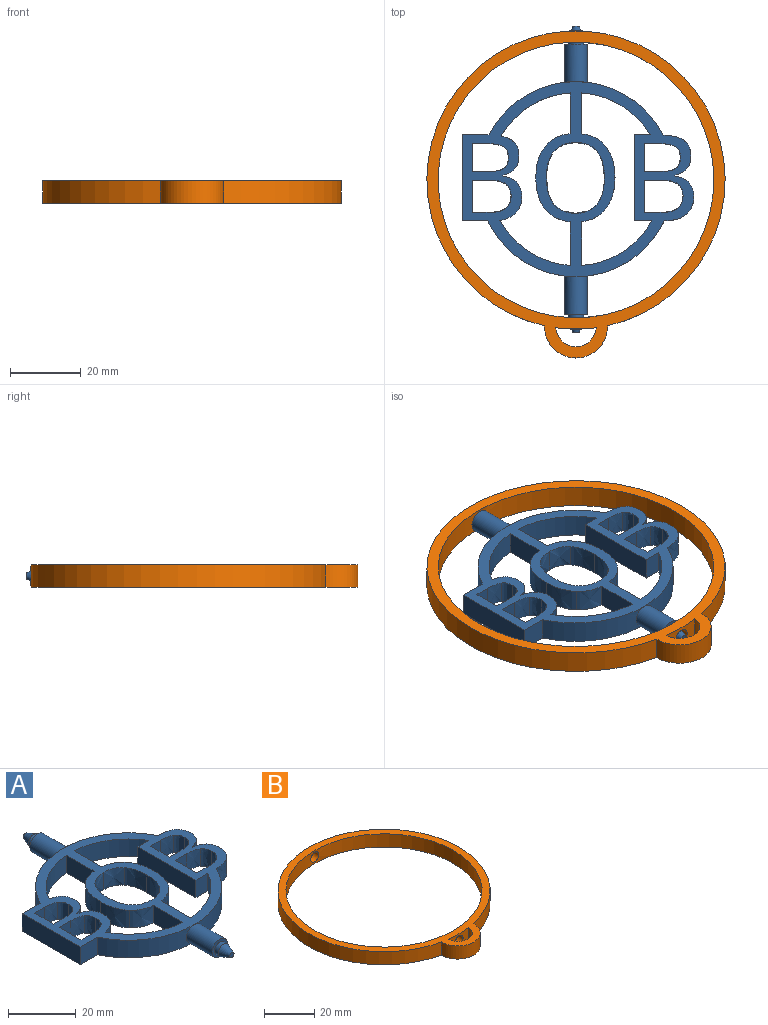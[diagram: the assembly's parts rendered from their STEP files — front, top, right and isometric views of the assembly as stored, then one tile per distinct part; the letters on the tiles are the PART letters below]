
ASSEMBLY  parts=2 mates=1
PART A: 91 faces, bbox 65.3x86.4x6.4 mm
  f0: cylinder r=27.5mm len=24.86mm, axis (0,0,1), area 181.3mm2, adj f34,f44,f45,f83
  f1: cylinder r=27.5mm len=24.5mm, axis (0,0,1), area 176.1mm2, adj f42,f44,f45,f82
  f2: extruded ~6.35x6.06mm, area 43.2mm2, adj f8,f44,f45,f75
  f3: extruded ~6.35x6.09mm, area 43.4mm2, adj f10,f44,f45,f76
  f4: cylinder r=24.36mm len=19.45mm, axis (0,0,1), area 151.6mm2, adj f19,f44,f45,f72
  f5: cylinder r=24.36mm len=19.84mm, axis (0,0,1), area 156.2mm2, adj f6,f18,f44,f45
  f6: plane 12.28x6.35mm, normal (-1,0,0), area 78mm2, adj f5,f9,f44,f45
  f7: extruded ~6.76x6.35mm, area 48.6mm2, adj f44,f45,f72,f79
  f8: extruded ~6.35x6.13mm, area 43.6mm2, adj f2,f44,f45,f74
  f9: extruded ~6.82x6.35mm, area 49.1mm2, adj f6,f44,f45,f80
  f10: extruded ~6.35x6.1mm, area 43.4mm2, adj f3,f44,f45,f73
  f11: cylinder r=24.36mm len=19.75mm, axis (0,0,1), area 155mm2, adj f15,f44,f45,f47
  f12: cylinder r=27.5mm len=24.86mm, axis (0,0,1), area 181.3mm2, adj f44,f45,f62,f83
  f13: cylinder r=24.36mm len=19.42mm, axis (0,0,1), area 150.2mm2, adj f44,f45,f60,f71
  f14: cylinder r=27.5mm len=24.51mm, axis (0,0,1), area 176.2mm2, adj f44,f45,f46,f82
  f15: plane 12.32x6.35mm, normal (1,0,0), area 78.2mm2, adj f11,f16,f44,f45
  f16: extruded ~6.46x6.35mm, area 47mm2, adj f15,f44,f45,f77
  f17: extruded ~6.52x6.35mm, area 47.3mm2, adj f44,f45,f71,f78
  f18: extruded ~6.35x3.96mm, area 27.6mm2, adj f5,f35,f44,f45
  f19: extruded ~6.35x2.89mm, area 19.7mm2, adj f4,f40,f44,f45
  f20: plane 9.08x6.35mm, normal (1,0,0), area 57.6mm2, adj f21,f43,f44,f45
  f21: plane 6.35x4.83mm, normal (0,-1,0), area 30.7mm2, adj f20,f22,f44,f45
  f22: extruded ~6.35x4.62mm, area 30.5mm2, adj f21,f23,f44,f45
  f23: extruded ~6.35x3.32mm, area 24.2mm2, adj f22,f24,f44,f45
  f24: extruded ~6.35x3.56mm, area 25.4mm2, adj f23,f25,f44,f45
  f25: extruded ~6.35x4.42mm, area 29.5mm2, adj f24,f43,f44,f45
  f26: plane 6.35x4.64mm, normal (0,1,0), area 29.5mm2, adj f27,f41,f44,f45
  f27: plane 7.94x6.35mm, normal (1,0,0), area 50.4mm2, adj f26,f28,f44,f45
  f28: plane 6.35x4.15mm, normal (0,-1,0), area 26.4mm2, adj f27,f29,f44,f45
  f29: extruded ~6.35x4.64mm, area 30.4mm2, adj f28,f30,f44,f45
  f30: extruded ~6.35x2.95mm, area 21.9mm2, adj f29,f31,f44,f45
  f31: extruded ~6.35x3.16mm, area 22.6mm2, adj f30,f41,f44,f45
  f32: plane 6.85x6.35mm, normal (0,1,0), area 43.5mm2, adj f33,f42,f44,f45
  f33: plane 24.25x6.35mm, normal (-1,0,0), area 154mm2, adj f32,f34,f44,f45
  f34: plane 7.21x6.35mm, normal (0,-1,0), area 45.8mm2, adj f0,f33,f44,f45
  f35: extruded ~6.35x5.07mm, area 36.4mm2, adj f18,f36,f44,f45
  f36: extruded ~6.35x5.81mm, area 56.4mm2, adj f35,f37,f44,f45
  f37: plane 6.35x0.16mm, normal (1,0,0), area 1mm2, adj f36,f38,f44,f45
  f38: extruded ~6.35x3.51mm, area 25.6mm2, adj f37,f39,f44,f45
  f39: extruded ~6.35x3.56mm, area 24.4mm2, adj f38,f40,f44,f45
  f40: extruded ~6.35x4.56mm, area 33.5mm2, adj f19,f39,f44,f45
  f41: extruded ~6.35x4.3mm, area 28.4mm2, adj f26,f31,f44,f45
  f42: extruded ~6.35x0.72mm, area 4.6mm2, adj f1,f32,f44,f45
  f43: plane 6.35x5.06mm, normal (0,1,0), area 32.2mm2, adj f20,f25,f44,f45
  f44: plane 65.27x54.99mm, normal (0,0,1), area 1015.6mm2, adj f0,f1,f2,f3,f4,f5,f6,f7
  f45: plane 65.27x54.99mm, normal (0,0,-1), area 1015.6mm2, adj f0,f1,f2,f3,f4,f5,f6,f7
  f46: extruded ~6.35x5.72mm, area 37.9mm2, adj f14,f44,f45,f68
  f47: plane 6.35x4.94mm, normal (0,-1,0), area 31.4mm2, adj f11,f44,f45,f61
  f48: plane 9.08x6.35mm, normal (1,0,0), area 57.6mm2, adj f44,f45,f49,f70
  f49: plane 6.35x4.83mm, normal (0,-1,0), area 30.7mm2, adj f44,f45,f48,f50
  f50: extruded ~6.35x4.62mm, area 30.5mm2, adj f44,f45,f49,f51
  f51: extruded ~6.35x3.32mm, area 24.2mm2, adj f44,f45,f50,f52
  f52: extruded ~6.35x3.56mm, area 25.4mm2, adj f44,f45,f51,f53
  f53: extruded ~6.35x4.42mm, area 29.5mm2, adj f44,f45,f52,f70
  f54: plane 6.35x4.64mm, normal (0,1,0), area 29.5mm2, adj f44,f45,f55,f69
  f55: plane 7.94x6.35mm, normal (1,0,0), area 50.4mm2, adj f44,f45,f54,f56
  f56: plane 6.35x4.15mm, normal (0,-1,0), area 26.4mm2, adj f44,f45,f55,f57
  f57: extruded ~6.35x4.64mm, area 30.4mm2, adj f44,f45,f56,f58
  f58: extruded ~6.35x2.95mm, area 21.9mm2, adj f44,f45,f57,f59
  f59: extruded ~6.35x3.16mm, area 22.6mm2, adj f44,f45,f58,f69
  f60: plane 6.35x4.52mm, normal (0,1,0), area 28.7mm2, adj f13,f44,f45,f61
  f61: plane 24.25x6.35mm, normal (-1,0,0), area 154mm2, adj f44,f45,f47,f60
  f62: extruded ~6.35x6.15mm, area 41.5mm2, adj f12,f44,f45,f63
  f63: extruded ~6.35x5.07mm, area 36.4mm2, adj f44,f45,f62,f64
  f64: extruded ~6.35x5.81mm, area 56.4mm2, adj f44,f45,f63,f65
  f65: plane 6.35x0.16mm, normal (1,0,0), area 1mm2, adj f44,f45,f64,f66
  f66: extruded ~6.35x3.51mm, area 25.6mm2, adj f44,f45,f65,f67
  f67: extruded ~6.35x3.56mm, area 24.4mm2, adj f44,f45,f66,f68
  f68: extruded ~6.35x4.56mm, area 33.5mm2, adj f44,f45,f46,f67
  f69: extruded ~6.35x4.3mm, area 28.4mm2, adj f44,f45,f54,f59
  f70: plane 6.35x5.06mm, normal (0,1,0), area 32.2mm2, adj f44,f45,f48,f53
  f71: plane 11.53x6.35mm, normal (1,0,0), area 73.2mm2, adj f13,f17,f44,f45
  f72: plane 11.5x6.35mm, normal (-1,0,0), area 73mm2, adj f4,f7,f44,f45
  f73: extruded ~7.47x6.35mm, area 50.3mm2, adj f10,f44,f45,f74
  f74: extruded ~7.4x6.35mm, area 49.8mm2, adj f8,f44,f45,f73
  f75: extruded ~7.42x6.35mm, area 49.8mm2, adj f2,f44,f45,f76
  f76: extruded ~7.48x6.35mm, area 50.2mm2, adj f3,f44,f45,f75
  f77: extruded ~9.16x6.35mm, area 62.5mm2, adj f16,f44,f45,f78
  f78: extruded ~9.16x6.35mm, area 62.4mm2, adj f17,f44,f45,f77
  f79: extruded ~9.18x6.35mm, area 62.6mm2, adj f7,f44,f45,f80
  f80: extruded ~9.25x6.35mm, area 63mm2, adj f9,f44,f45,f79
  f81: plane 6.35x6.35mm, normal (0,1,0), area 17mm2, adj f82,f88
  f82: cylinder r=3.17mm len=10.79mm, axis (0,1,0), area 213.4mm2, adj f1,f14,f81
  f83: cylinder r=3.17mm len=10.79mm, axis (0,1,0), area 213.4mm2, adj f0,f12,f84
  f84: plane 6.35x6.35mm, normal (0,-1,0), area 17mm2, adj f83,f85
  f85: cylinder r=2.16mm len=4.32mm, axis (0,1,0), area 21.6mm2, adj f84,f87
  f86: plane 1.78x1.78mm, normal (0,-1,0), area 2.5mm2, adj f87
  f87: cone r=0.89mm half-angle=20deg, axis (0,1,0), area 35.6mm2, adj f85,f86
  f88: cylinder r=2.16mm len=4.32mm, axis (0,-1,0), area 21.6mm2, adj f81,f90
  f89: plane 1.78x1.78mm, normal (0,1,0), area 2.5mm2, adj f90
  f90: cone r=2.16mm half-angle=20deg, axis (0,-1,0), area 35.6mm2, adj f88,f89
PART B: 9 faces, bbox 84.1x92.2x6.4 mm
  f0: cylinder r=42.04mm len=11.42mm, axis (0,0,-1), area 56.3mm2, adj f3,f4,f5,f7
  f1: cylinder r=42.04mm len=84.07mm, axis (0,0,-1), area 1546.9mm2, adj f3,f4,f6,f8
  f2: cylinder r=38.86mm len=77.72mm, axis (0,0,-1), area 1517.6mm2, adj f3,f4,f5,f6
  f3: plane 92.21x84.07mm, normal (0,0,1), area 879.1mm2, adj f0,f1,f2,f7,f8
  f4: plane 92.21x84.07mm, normal (0,0,-1), area 879.1mm2, adj f0,f1,f2,f7,f8
  f5: cylinder r=2.29mm len=4.57mm, axis (0,-1,0), area 45.6mm2, adj f0,f2
  f6: cylinder r=2.29mm len=4.57mm, axis (0,-1,0), area 45.6mm2, adj f1,f2
  f7: cylinder r=5.72mm len=11.42mm, axis (0,0,1), area 109.4mm2, adj f0,f3,f4
  f8: cylinder r=8.9mm len=17.79mm, axis (0,0,1), area 179.9mm2, adj f1,f3,f4
PLACE A rot(axis=(0,-1,0),0.1deg) t=(-30,-13.39,-3.72)mm
PLACE B t=(-30,-13.62,-3.72)mm fixed
MATE revolute A.f82 <-> B.f5  axis (0,-1,0) through (-30,-51.49,-0.55)mm
